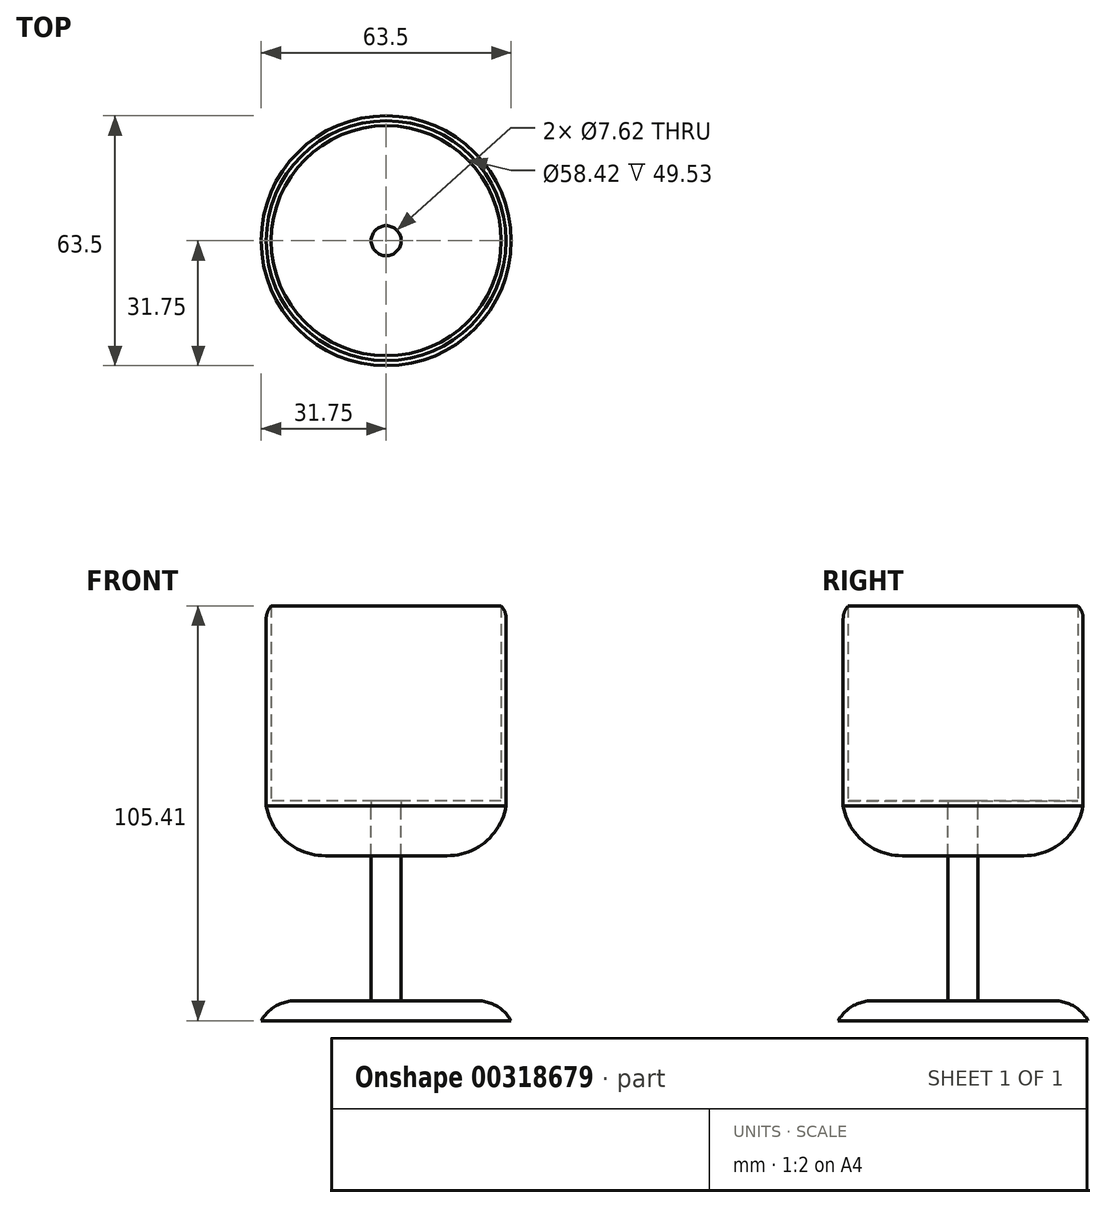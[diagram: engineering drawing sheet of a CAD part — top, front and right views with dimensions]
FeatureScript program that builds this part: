
annotation { "Feature Type Name" : "Feature", "Feature Type Description" : "" }
export const myFeature = defineFeature(function(context is Context, id is Id, definition is map)
    precondition{}
    {
        {
            var Q0;
            Q0=qCreatedBy(makeId("Top.planeOp"),FACE);
            var sketch = newSketch(context, id + "F0", { "sketchPlane" : qUnion([Q0])});
            skCircle(sketch, "E0", {"center": v(0, 0) * mm, "radius": 31.75 * mm});
            skSolve(sketch);
        }
        {
            var Q0;
            Q0=makeQuery(id+"F0.imprint","IMPRINT",FACE,{"disambiguationData":[TD([[makeQuery(id+"F0.imprint","IMPRINT",EDGE,{"derivedFrom":sQuery(id+"F0.wireOp",EDGE,"E0")}),1.0]])]});
            extrude(context, id + "F1", {"entities" : qUnion([Q0]), "depth" : 5.08 * mm});
        }
        {
            var Q0;
            Q0=makeQuery(id+"F1.opExtrude","CAP_FACE",FACE,{"disambiguationData":[OSD([sQuery(id+"F0.wireOp",EDGE,"E0")])],"isStart":false});
            fillet(context, id + "F2", {"entities" : qUnion([Q0]), "radius" : 10.16 * mm, "tangentPropagation" : true, "allowEdgeOverflow" : false});
        }
        {
            var Q0;
            Q0=makeQuery(id+"F1.opExtrude","CAP_FACE",FACE,{"disambiguationData":[OSD([sQuery(id+"F0.wireOp",EDGE,"E0")])],"isStart":false});
            var sketch = newSketch(context, id + "F3", { "sketchPlane" : qUnion([Q0])});
            skCircle(sketch, "E1", {"center": v(0, 0) * mm, "radius": 3.8 * mm});
            skSolve(sketch);
        }
        {
            var Q0;
            Q0=makeQuery(id+"F3.imprint","IMPRINT",FACE,{"disambiguationData":[TD([[makeQuery(id+"F3.imprint","IMPRINT",EDGE,{"derivedFrom":sQuery(id+"F3.wireOp",EDGE,"E1")}),1.0]])]});
            extrude(context, id + "F4", {"entities" : qUnion([Q0]), "operationType" : NewBodyOperationType.ADD, "depth" : 49.53 * mm});
        }
        {
            var Q0;
            Q0=makeQuery(id+"F4.opExtrude","CAP_FACE",FACE,{"disambiguationData":[OSD([sQuery(id+"F3.wireOp",EDGE,"E1")])],"isStart":false});
            var sketch = newSketch(context, id + "F5", { "sketchPlane" : qUnion([Q0])});
            skCircle(sketch, "E2", {"center": v(0, 0) * mm, "radius": 30.48 * mm});
            skSolve(sketch);
        }
        {
            var Q0;
            Q0=makeQuery(id+"F5.imprint","IMPRINT",FACE,{"disambiguationData":[TD([[makeQuery(id+"F5.imprint","IMPRINT",EDGE,{"derivedFrom":sQuery(id+"F5.wireOp",EDGE,"E2")}),1.0]])]});
            extrude(context, id + "F6", {"entities" : qUnion([Q0]), "depth" : 50.8 * mm});
        }
        {
            var Q0;
            Q0=makeQuery(id+"F6.opExtrude","CAP_FACE",FACE,{"disambiguationData":[OSD([sQuery(id+"F3.wireOp",EDGE,"E1"),sQuery(id+"F5.wireOp",EDGE,"E2")])],"isStart":true});
            extrude(context, id + "F7", {"entities" : qUnion([Q0]), "depth" : 12.7 * mm});
        }
        {
            var Q0;
            Q0=makeQuery(id+"F7.opExtrude","CAP_EDGE",EDGE,{"disambiguationData":[OSD([sQuery(id+"F5.wireOp",EDGE,"E2")])],"isStart":false});
            fillet(context, id + "F8", {"entities" : qUnion([Q0]), "radius" : 15.24 * mm, "tangentPropagation" : true, "allowEdgeOverflow" : false});
        }
        {
            var Q0;
            Q0=makeQuery(id+"F6.opExtrude","CAP_FACE",FACE,{"disambiguationData":[OSD([sQuery(id+"F3.wireOp",EDGE,"E1"),sQuery(id+"F5.wireOp",EDGE,"E2")])],"isStart":false});
            var Q1;
            Q1=makeQuery(id+"F6.opExtrude","SWEPT_FACE",FACE,{"disambiguationData":[OSD([sQuery(id+"F3.wireOp",EDGE,"E1")])]});
            shell(context, id + "F9", {"entities" : qUnion([Q0, Q1]), "thickness" : 1.27 * mm});
        }
        {
            var Q0;
            Q0=makeQuery(id+"F6.opExtrude","CAP_EDGE",EDGE,{"disambiguationData":[OSD([sQuery(id+"F5.wireOp",EDGE,"E2")])],"isStart":false});
            fillet(context, id + "F10", {"entities" : qUnion([Q0]), "radius" : 5.08 * mm, "tangentPropagation" : true, "allowEdgeOverflow" : false});
        }
    });
